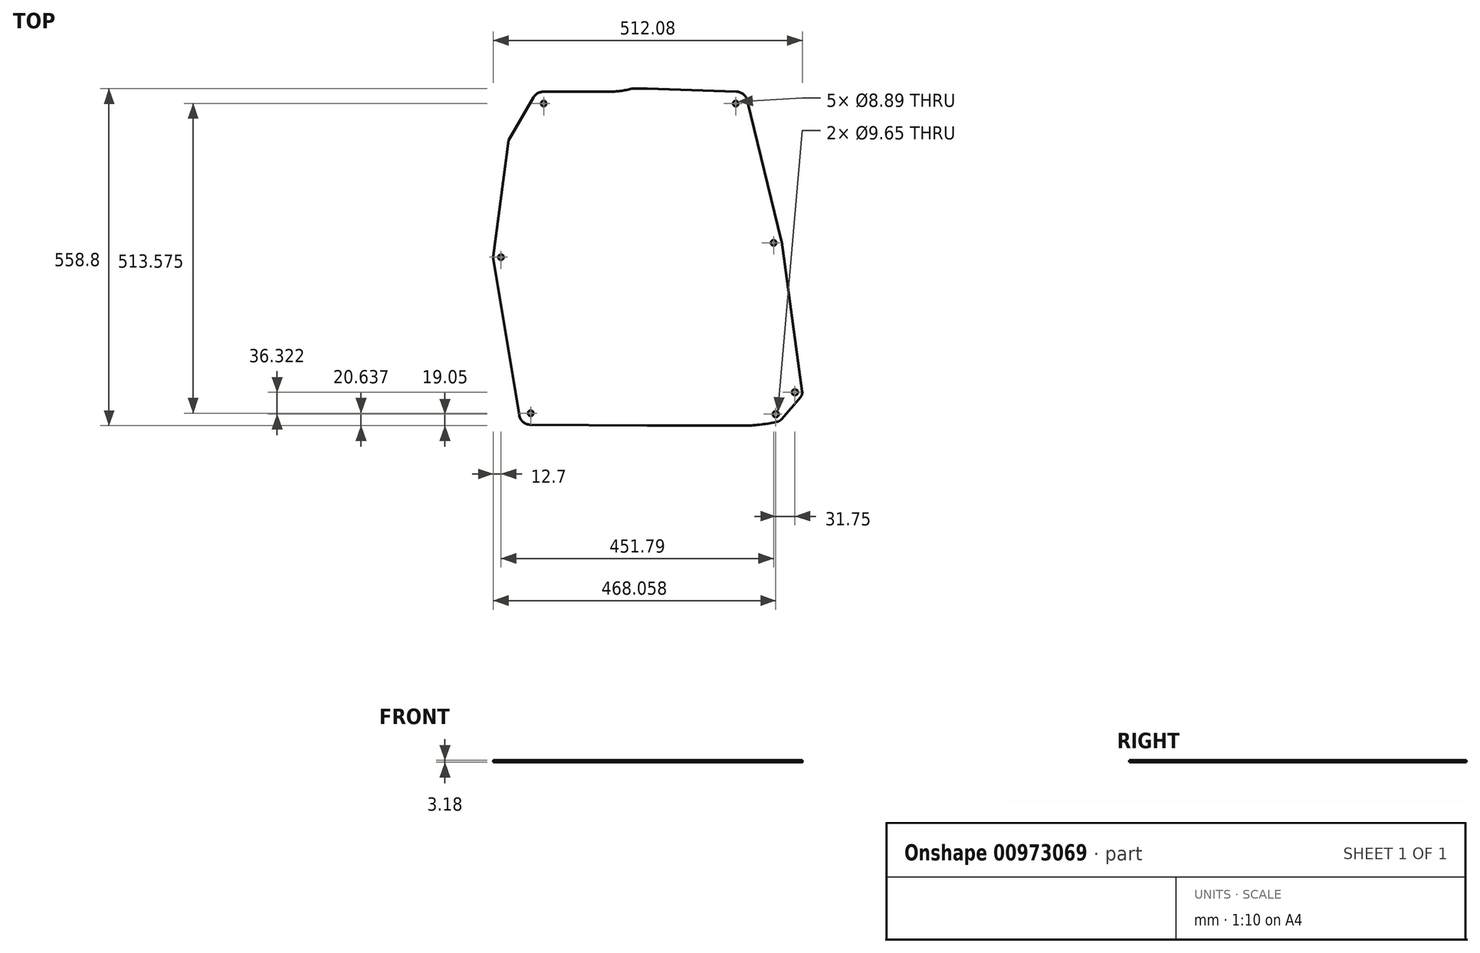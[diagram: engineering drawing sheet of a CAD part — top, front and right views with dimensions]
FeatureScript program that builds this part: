
annotation { "Feature Type Name" : "Feature", "Feature Type Description" : "" }
export const myFeature = defineFeature(function(context is Context, id is Id, definition is map)
    precondition{}
    {
        {
            var Q0;
            Q0=qCreatedBy(makeId("Top.planeOp"),FACE);
            var sketch = newSketch(context, id + "F0", { "sketchPlane" : qUnion([Q0])});
            skLineSegment(sketch, "E0", {"start": v(0, 0) * mm, "end": v(0, 558.8) * mm, "construction": true});
            skLineSegment(sketch, "E1", {"start": v(0, 20.64) * mm, "end": v(-188.91, 20.64) * mm, "construction": true});
            skLineSegment(sketch, "E2", {"start": v(0, 19.05) * mm, "end": v(207.96, 19.05) * mm, "construction": true});
            skLineSegment(sketch, "E3", {"start": v(0, 55.37) * mm, "end": v(239.71, 55.37) * mm, "construction": true});
            skLineSegment(sketch, "E4", {"start": v(0, 279.4) * mm, "end": v(-238.13, 279.4) * mm, "construction": true});
            skLineSegment(sketch, "E5", {"start": v(0, 303.21) * mm, "end": v(204.77, 303.21) * mm, "construction": true});
            skLineSegment(sketch, "E6", {"start": v(0, 473.08) * mm, "end": v(-230.17, 473.08) * mm, "construction": true});
            skLineSegment(sketch, "E7", {"start": v(0, 534.21) * mm, "end": v(-167.39, 534.21) * mm, "construction": true});
            skLineSegment(sketch, "E8", {"start": v(0, 534.21) * mm, "end": v(141.99, 534.21) * mm, "construction": true});
            skCircle(sketch, "E9", {"center": v(-171.83, 534.21) * mm, "radius": 4.45 * mm});
            skCircle(sketch, "E10", {"center": v(146.43, 534.21) * mm, "radius": 4.45 * mm});
            skCircle(sketch, "E11", {"center": v(-242.57, 279.4) * mm, "radius": 4.45 * mm});
            skCircle(sketch, "E12", {"center": v(209.22, 303.21) * mm, "radius": 4.45 * mm});
            skCircle(sketch, "E13", {"center": v(-193.36, 20.64) * mm, "radius": 4.45 * mm});
            skCircle(sketch, "E14", {"center": v(212.79, 19.05) * mm, "radius": 4.83 * mm});
            skCircle(sketch, "E15", {"center": v(244.54, 55.37) * mm, "radius": 4.83 * mm});
            skCircle(sketch, "E16", {"center": v(-193.36, 20.64) * mm, "radius": 19.18 * mm});
            skCircle(sketch, "E17", {"center": v(212.79, 19.05) * mm, "radius": 12.75 * mm});
            skCircle(sketch, "E18", {"center": v(244.54, 55.37) * mm, "radius": 12.27 * mm});
            skCircle(sketch, "E19", {"center": v(209.22, 303.21) * mm, "radius": 13.46 * mm});
            skCircle(sketch, "E20", {"center": v(-242.57, 279.4) * mm, "radius": 12.7 * mm});
            skCircle(sketch, "E21", {"center": v(-171.83, 534.21) * mm, "radius": 19.69 * mm});
            skCircle(sketch, "E22", {"center": v(146.43, 534.21) * mm, "radius": 19.94 * mm});
            skLineSegment(sketch, "E23", {"start": v(0, 0) * mm, "end": v(-193.5, 1.46) * mm});
            skLineSegment(sketch, "E24", {"start": v(222.46, 305.73) * mm, "end": v(256.7, 57.04) * mm});
            skLineSegment(sketch, "E25", {"start": v(165.8, 538.92) * mm, "end": v(222.46, 305.73) * mm});
            skLineSegment(sketch, "E26.trimOffspring", {"start": v(222.47, 10.75) * mm, "end": v(253.86, 47.4) * mm});
            skLineSegment(sketch, "E27", {"start": v(-212.28, 17.52) * mm, "end": v(-255.1, 277.33) * mm});
            skLineSegment(sketch, "E28", {"start": v(-230.17, 473.08) * mm, "end": v(-255.16, 281.04) * mm});
            skLineSegment(sketch, "E29", {"start": v(-230.17, 473.07) * mm, "end": v(-188.85, 544.11) * mm});
            skLineSegment(sketch, "E30", {"start": v(-171.83, 534.21) * mm, "end": v(-171.83, 553.9) * mm});
            skLineSegment(sketch, "E31", {"start": v(-171.83, 553.9) * mm, "end": v(-63.88, 553.9) * mm});
            skLineSegment(sketch, "E32", {"start": v(0, 558.8) * mm, "end": v(147.06, 554.14) * mm});
            skLineSegment(sketch, "E33", {"start": v(0, 558.8) * mm, "end": v(-25.4, 558.8) * mm});
            skArc(sketch, "E34", {"start": v(-63.88, 553.9) * mm, "mid": v(-44.49, 555.13) * mm, "end": v(-25.4, 558.8) * mm});
            skLineSegment(sketch, "E35", {"start": v(0, 0) * mm, "end": v(158.75, 0) * mm});
            skArc(sketch, "E36", {"start": v(158.75, 0) * mm, "mid": v(186.14, 1.58) * mm, "end": v(213.17, 6.3) * mm});
            skSolve(sketch);
        }
        {
            var Q0;
            {var subQ16=sQuery(id+"F0.wireOp",EDGE,"E23");Q0=makeQuery(id+"F0.imprint","IMPRINT",FACE,{"disambiguationData":[TD([[makeQuery(id+"F0.imprint","IMPRINT",EDGE,{"derivedFrom":subQ16}),-1.0]])]});}
            var Q1;
            Q1=makeQuery(id+"F0.imprint","IMPRINT",FACE,{"disambiguationData":[TD([[makeQuery(id+"F0.imprint","IMPRINT",EDGE,{"derivedFrom":sQuery(id+"F0.wireOp",EDGE,"E13")}),-1.0]])]});
            var Q2;
            Q2=makeQuery(id+"F0.imprint","IMPRINT",FACE,{"disambiguationData":[TD([[makeQuery(id+"F0.imprint","IMPRINT",EDGE,{"derivedFrom":sQuery(id+"F0.wireOp",EDGE,"E11")}),-1.0]])]});
            var Q3;
            Q3=makeQuery(id+"F0.imprint","IMPRINT",FACE,{"disambiguationData":[TD([[makeQuery(id+"F0.imprint","IMPRINT",EDGE,{"derivedFrom":sQuery(id+"F0.wireOp",EDGE,"E12")}),-1.0]])]});
            var Q4;
            Q4=makeQuery(id+"F0.imprint","IMPRINT",FACE,{"disambiguationData":[TD([[makeQuery(id+"F0.imprint","IMPRINT",EDGE,{"derivedFrom":sQuery(id+"F0.wireOp",EDGE,"E15")}),-1.0]])]});
            var Q5;
            Q5=makeQuery(id+"F0.imprint","IMPRINT",FACE,{"disambiguationData":[TD([[makeQuery(id+"F0.imprint","IMPRINT",EDGE,{"derivedFrom":sQuery(id+"F0.wireOp",EDGE,"E14")}),-1.0]])]});
            var Q6;
            Q6=makeQuery(id+"F0.imprint","IMPRINT",FACE,{"disambiguationData":[TD([[makeQuery(id+"F0.imprint","IMPRINT",EDGE,{"derivedFrom":sQuery(id+"F0.wireOp",EDGE,"E10")}),-1.0]])]});
            var Q7;
            Q7=makeQuery(id+"F0.imprint","IMPRINT",FACE,{"disambiguationData":[TD([[makeQuery(id+"F0.imprint","IMPRINT",EDGE,{"derivedFrom":sQuery(id+"F0.wireOp",EDGE,"E9")}),-1.0]])]});
            extrude(context, id + "F1", {"entities" : qUnion([Q0, Q1, Q2, Q3, Q4, Q5, Q6, Q7]), "depth" : 3.17 * mm, "offsetDistance" : 25.4 * mm});
        }
    });
